# Revit family: F1AR_2511-2543-2606_OS275
name_source: partatom
category: Finestre
units: mm (PartAtom-declared; Revit-internal decimal feet)

## family parameters
Condiviso = No
Host = Muro
Numero OmniClass = 23.30.20.00
Punto di calcolo locali = No
Sempre verticale = Sì
Taglio con vuoti quando caricato = No
Titolo OmniClass = Windows

## types (4) — shared parameters
Altezza = 2000 mm  [stored 6.56168 ft]
Altezza di default del davanzale = 800 mm
Chiusura muro = Per host
Costruzione analitica = <Nessuno>
Descrizione = Finestra 1 anta e ribalta
H = 2000 mm  [stored 6.56168 ft]
H1 = 2000 mm  [stored 6.56168 ft]
H_Max = 3000 mm  [stored 9.84252 ft]
H_Min = 670 mm  [stored 2.19816 ft]
H_fermavetro = 1936 mm  [stored 6.35171 ft]
H_man = 1050 mm  [stored 3.44488 ft]
H_maniglia = 1050 mm  [stored 3.44488 ft]
H_vetro = 1924 mm  [stored 6.31234 ft]
L_Max = 1400 mm  [stored 4.59318 ft]
L_Min = 600 mm
Maniglia_alta = 1050 mm  [stored 3.44488 ft]
Maniglia_bassa = 1000 mm  [stored 3.28084 ft]
Maniglia_media = 500 mm  [stored 1.64042 ft]
Modello = OS2 75
Produttore = Secco Sistemi Spa
URL = https://www.seccosistemi.com
WARNING = No
altezza maniglia = 500 mm  [stored 1.64042 ft]
n2_scarichi = 2
n3_scarichi = 3
numero_scarichi = 3

## per-type parameters (varying)
| type | L | L1 | L_fermavetro | L_vetro | Larghezza | MATERIALE |
| Ottone | 1000 mm  [stored 3.28084 ft] | 1000 mm  [stored 3.28084 ft] | 936 mm  [stored 3.07087 ft] | 924 mm  [stored 3.0315 ft] | 1000 mm  [stored 3.28084 ft] | Ottone |
| Acciaio inox | 900 mm  [stored 2.95276 ft] | 900 mm  [stored 2.95276 ft] | 836 mm  [stored 2.74278 ft] | 824 mm  [stored 2.70341 ft] | 900 mm  [stored 2.95276 ft] | Acciaio inox, spazzolato |
| Acciaio zincato | 1000 mm  [stored 3.28084 ft] | 1000 mm  [stored 3.28084 ft] | 936 mm  [stored 3.07087 ft] | 924 mm  [stored 3.0315 ft] | 1000 mm  [stored 3.28084 ft] | Acciaio zincato |
| Acciaio corten | 1000 mm  [stored 3.28084 ft] | 1000 mm  [stored 3.28084 ft] | 936 mm  [stored 3.07087 ft] | 924 mm  [stored 3.0315 ft] | 1000 mm  [stored 3.28084 ft] | Acciaio corten |

note: [stored X ft] marks values corroborated as IEEE doubles in the binary element streams (Revit-internal decimal feet)
